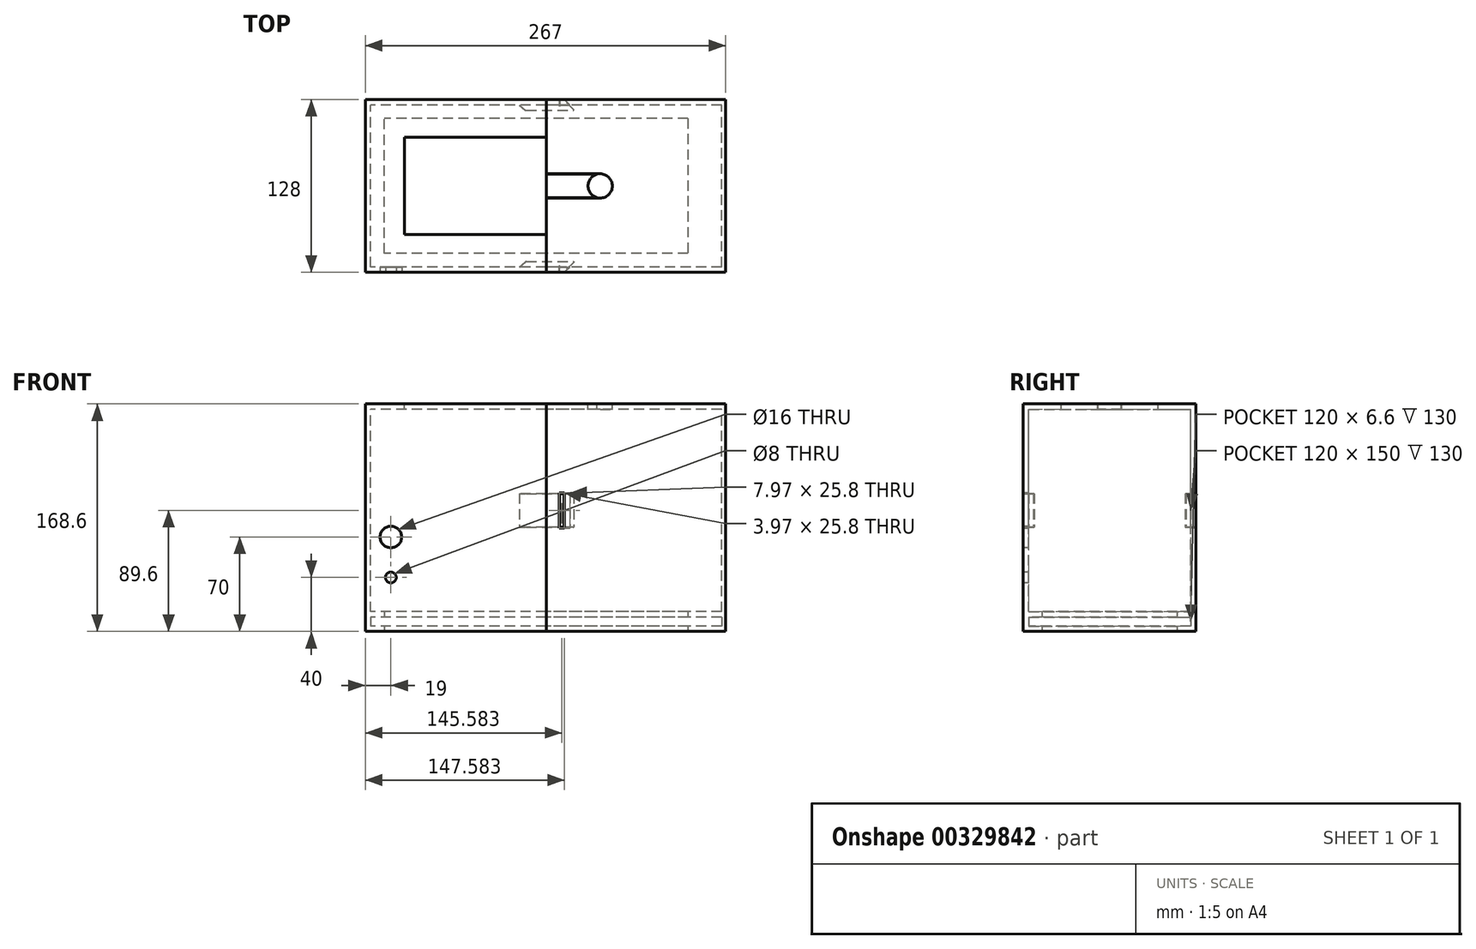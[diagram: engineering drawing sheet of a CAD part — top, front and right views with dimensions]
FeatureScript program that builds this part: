
annotation { "Feature Type Name" : "Feature", "Feature Type Description" : "" }
export const myFeature = defineFeature(function(context is Context, id is Id, definition is map)
    precondition{}
    {
        {
            assignVariable(context, id + "F0", {"name" : "InsideHeight", "anyValue" : 150});
        }
        {
            assignVariable(context, id + "F1", {"name" : "WallThickness", "anyValue" : 4});
        }
        {
            assignVariable(context, id + "F2", {"name" : "SlideGap", "anyValue" : 0.4});
        }
        {
            var Q0;
            Q0=qCreatedBy(makeId("Right.planeOp"),FACE);
            var sketch = newSketch(context, id + "F3", { "sketchPlane" : qUnion([Q0])});
            skLineSegment(sketch, "E0.top", {"start": v(0, 154) * mm, "end": v(64, 154) * mm});
            skLineSegment(sketch, "E0.left", {"start": v(0, 0) * mm, "end": v(0, 154) * mm});
            skLineSegment(sketch, "E1", {"start": v(4, 0) * mm, "end": v(4, 150) * mm});
            skLineSegment(sketch, "E2", {"start": v(4, 150) * mm, "end": v(64, 150) * mm});
            skLineSegment(sketch, "E3", {"start": v(4, 0) * mm, "end": v(14, 0) * mm});
            skLineSegment(sketch, "E4", {"start": v(14, 0) * mm, "end": v(14, -4) * mm});
            skLineSegment(sketch, "E5", {"start": v(14, -4) * mm, "end": v(4, -4) * mm});
            skLineSegment(sketch, "E6", {"start": v(4, -4) * mm, "end": v(4, -10.6) * mm});
            skLineSegment(sketch, "E7", {"start": v(4, -10.6) * mm, "end": v(14, -10.6) * mm});
            skLineSegment(sketch, "E8", {"start": v(14, -10.6) * mm, "end": v(14, -14.6) * mm});
            skLineSegment(sketch, "E9", {"start": v(14, -14.6) * mm, "end": v(0, -14.6) * mm});
            skLineSegment(sketch, "E10", {"start": v(0, -14.6) * mm, "end": v(0, 0) * mm});
            skLineSegment(sketch, "E11", {"start": v(64, 154) * mm, "end": v(64, 150) * mm, "construction": true});
            skLineSegment(sketch, "E12.MirrorCS", {"start": v(128, 154) * mm, "end": v(64, 154) * mm});
            skLineSegment(sketch, "E13.MirrorCS", {"start": v(124, 150) * mm, "end": v(64, 150) * mm});
            skLineSegment(sketch, "E14.MirrorCS", {"start": v(124, 0) * mm, "end": v(124, 150) * mm});
            skLineSegment(sketch, "E15.MirrorCS", {"start": v(128, 0) * mm, "end": v(128, 154) * mm});
            skLineSegment(sketch, "E16.MirrorCS", {"start": v(128, -14.6) * mm, "end": v(128, 0) * mm});
            skLineSegment(sketch, "E17.MirrorCS", {"start": v(114, -14.6) * mm, "end": v(128, -14.6) * mm});
            skLineSegment(sketch, "E18.MirrorCS", {"start": v(114, -10.6) * mm, "end": v(114, -14.6) * mm});
            skLineSegment(sketch, "E19.MirrorCS", {"start": v(124, -10.6) * mm, "end": v(114, -10.6) * mm});
            skLineSegment(sketch, "E20.MirrorCS", {"start": v(124, -4) * mm, "end": v(124, -10.6) * mm});
            skLineSegment(sketch, "E21.MirrorCS", {"start": v(114, -4) * mm, "end": v(124, -4) * mm});
            skLineSegment(sketch, "E22.MirrorCS", {"start": v(114, 0) * mm, "end": v(114, -4) * mm});
            skLineSegment(sketch, "E23.MirrorCS", {"start": v(124, 0) * mm, "end": v(114, 0) * mm});
            skLineSegment(sketch, "E24", {"start": v(4, -7.3) * mm, "end": v(0, -7.3) * mm, "construction": true});
            skSolve(sketch);
        }
        {
            var Q0;
            Q0 = qSketchRegion(id + "F3", true);
            extrude(context, id + "F4", {"entities" : qUnion([Q0]), "depth" : 130 * mm, "offsetDistance" : 25 * mm});
        }
        {
            var Q0;
            Q0=makeQuery(id+"F4.opExtrude","CAP_FACE",FACE,{"disambiguationData":[OSD([sQuery(id+"F3.wireOp",EDGE,"E0.top"),sQuery(id+"F3.wireOp",EDGE,"E0.left"),sQuery(id+"F3.wireOp",EDGE,"E0.right"),sQuery(id+"F3.wireOp",EDGE,"8XVz9hmB-15gg-s7JK-XLWV-TxlLlYY56E4R"),sQuery(id+"F3.wireOp",EDGE,"E1"),sQuery(id+"F3.wireOp",EDGE,"E2"),sQuery(id+"F3.wireOp",EDGE,"x6d7EpG5-ogLQ-dseG-wOhr-lL4PzdnoVMk9"),sQuery(id+"F3.wireOp",EDGE,"GP6dVw60-cyKg-IaOy-Ul32-FflkX6cR7JPA")])],"isStart":true});
            var sketch = newSketch(context, id + "F5", { "sketchPlane" : qUnion([Q0])});
            skLineSegment(sketch, "E25.bottom", {"start": v(0, 154) * mm, "end": v(-128, 154) * mm});
            skLineSegment(sketch, "E25.top", {"start": v(0, -14.6) * mm, "end": v(-128, -14.6) * mm});
            skLineSegment(sketch, "E25.left", {"start": v(0, 154) * mm, "end": v(0, -14.6) * mm});
            skLineSegment(sketch, "E25.right", {"start": v(-128, 154) * mm, "end": v(-128, -14.6) * mm});
            skSolve(sketch);
        }
        {
            var Q0;
            Q0 = qSketchRegion(id + "F5", true);
            extrude(context, id + "F6", {"entities" : qUnion([Q0]), "operationType" : NewBodyOperationType.ADD, "depth" : (getVariable(context, 'WallThickness')) * mm, "offsetDistance" : 25 * mm});
        }
        {
            var Q0;
            Q0=makeQuery(id+"F4.opExtrude","SWEPT_FACE",FACE,{"disambiguationData":[OSD([sQuery(id+"F3.wireOp",EDGE,"E2"),sQuery(id+"F3.wireOp",EDGE,"E13.MirrorCS")])]});
            cPlane(context, id + "F7", {"entities" : qUnion([Q0]), "cplaneType" : CPlaneType.OFFSET, "offset" : (getVariable(context, 'InsideHeight') / 2) * mm, "width" : 150 * mm, "height" : 150 * mm});
        }
        {
            var Q0;
            Q0=qCreatedBy(id+"F7.planeOp",FACE);
            var sketch = newSketch(context, id + "F8", { "sketchPlane" : qUnion([Q0])});
            skLineSegment(sketch, "E26", {"start": v(130, -120) * mm, "end": v(150.5, -120) * mm});
            skLineSegment(sketch, "E27", {"start": v(150.5, -120) * mm, "end": v(150.5, -120.5) * mm});
            skLineSegment(sketch, "E28", {"start": v(150.5, -120.5) * mm, "end": v(143, -128) * mm});
            skLineSegment(sketch, "E29", {"start": v(140, -128) * mm, "end": v(140, -124) * mm});
            skLineSegment(sketch, "E30", {"start": v(140, -124) * mm, "end": v(130, -124) * mm});
            skLineSegment(sketch, "E31", {"start": v(-4, -64) * mm, "end": v(0, -64) * mm, "construction": true});
            skLineSegment(sketch, "E32", {"start": v(140, -128) * mm, "end": v(143, -128) * mm});
            skPoint(sketch, "E33.orphan", {"position": v(140, -131) * mm});
            skLineSegment(sketch, "E34", {"start": v(130, -124) * mm, "end": v(110, -124) * mm});
            skLineSegment(sketch, "E35", {"start": v(110, -124) * mm, "end": v(115, -120) * mm});
            skLineSegment(sketch, "E36", {"start": v(115, -120) * mm, "end": v(130, -120) * mm});
            skLineSegment(sketch, "E37.MirrorCS", {"start": v(150.5, -7.5) * mm, "end": v(143, 0) * mm});
            skLineSegment(sketch, "E38.MirrorCS", {"start": v(140, 0) * mm, "end": v(143, 0) * mm});
            skLineSegment(sketch, "E39.MirrorCS", {"start": v(140, 0) * mm, "end": v(140, -4) * mm});
            skLineSegment(sketch, "E40.MirrorCS", {"start": v(140, -4) * mm, "end": v(130, -4) * mm});
            skLineSegment(sketch, "E41.MirrorCS", {"start": v(130, -4) * mm, "end": v(110, -4) * mm});
            skLineSegment(sketch, "E42.MirrorCS", {"start": v(110, -4) * mm, "end": v(115, -8) * mm});
            skLineSegment(sketch, "E43.MirrorCS", {"start": v(115, -8) * mm, "end": v(130, -8) * mm});
            skLineSegment(sketch, "E44.MirrorCS", {"start": v(130, -8) * mm, "end": v(150.5, -8) * mm});
            skLineSegment(sketch, "E45.MirrorCS", {"start": v(150.5, -8) * mm, "end": v(150.5, -7.5) * mm});
            skSolve(sketch);
        }
        {
            var Q0;
            Q0 = qSketchRegion(id + "F8", true);
            var Q1;
            Q1=makeQuery(id+"F6.boolean.opBoolean","MERGE",FACE,{"derivedFrom":[makeQuery(id+"F4.opExtrude","SWEPT_FACE",FACE,{"disambiguationData":[OSD([sQuery(id+"F3.wireOp",EDGE,"E0.top")])]}),makeQuery(id+"F6.opExtrude","SWEPT_FACE",FACE,{"disambiguationData":[OSD([sQuery(id+"F5.wireOp",EDGE,"WYE85QNL-GnE7-bL8G-Y7DR-a2gwiA7N3Xrg.bottom")])]})]});
            extrude(context, id + "F9", {"entities" : qUnion([Q0]), "operationType" : NewBodyOperationType.ADD, "oppositeDirection" : true, "depth" : 25 * mm, "endBoundEntityFace" : qUnion([Q1]), "offsetDistance" : 25 * mm, "symmetric" : true});
        }
        {
            var Q0;
            Q0=makeQuery(id+"F6.boolean.opBoolean","MERGE",FACE,{"derivedFrom":[makeQuery(id+"F4.opExtrude","SWEPT_FACE",FACE,{"disambiguationData":[OSD([sQuery(id+"F3.wireOp",EDGE,"E0.left"),sQuery(id+"F3.wireOp",EDGE,"E10")])]}),makeQuery(id+"F6.opExtrude","SWEPT_FACE",FACE,{"disambiguationData":[OSD([sQuery(id+"F5.wireOp",EDGE,"E25.left")])]})]});
            var sketch = newSketch(context, id + "F10", { "sketchPlane" : qUnion([Q0])});
            skCircle(sketch, "E46", {"center": v(15, 25.4) * mm, "radius": 4 * mm});
            skLineSegment(sketch, "E47", {"start": v(15, 25.4) * mm, "end": v(15, 55.4) * mm, "construction": true});
            skCircle(sketch, "E48", {"center": v(15, 55.4) * mm, "radius": 8 * mm});
            skSolve(sketch);
        }
        {
            var Q0;
            Q0 = qSketchRegion(id + "F10", true);
            extrude(context, id + "F11", {"entities" : qUnion([Q0]), "operationType" : NewBodyOperationType.REMOVE, "endBound" : BoundingType.UP_TO_NEXT, "oppositeDirection" : true, "depth" : 25 * mm, "offsetDistance" : 25 * mm});
        }
        {
            var Q0;
            Q0=makeQuery(id+"F6.opExtrude","CAP_FACE",FACE,{"disambiguationData":[OSD([sQuery(id+"F5.wireOp",EDGE,"E25.bottom"),sQuery(id+"F5.wireOp",EDGE,"E25.top"),sQuery(id+"F5.wireOp",EDGE,"E25.left"),sQuery(id+"F5.wireOp",EDGE,"E25.right")])],"isStart":true});
            var sketch = newSketch(context, id + "F12", { "sketchPlane" : qUnion([Q0])});
            skLineSegment(sketch, "E49.bottom", {"start": v(14, 0) * mm, "end": v(114, 0) * mm});
            skLineSegment(sketch, "E49.top", {"start": v(14, -4) * mm, "end": v(114, -4) * mm});
            skLineSegment(sketch, "E49.left", {"start": v(14, 0) * mm, "end": v(14, -4) * mm});
            skLineSegment(sketch, "E49.right", {"start": v(114, 0) * mm, "end": v(114, -4) * mm});
            skLineSegment(sketch, "E50.bottom", {"start": v(114, -10.6) * mm, "end": v(14, -10.6) * mm});
            skLineSegment(sketch, "E50.top", {"start": v(114, -14.6) * mm, "end": v(14, -14.6) * mm});
            skLineSegment(sketch, "E50.left", {"start": v(114, -10.6) * mm, "end": v(114, -14.6) * mm});
            skLineSegment(sketch, "E50.right", {"start": v(14, -10.6) * mm, "end": v(14, -14.6) * mm});
            skSolve(sketch);
        }
        {
            var Q0;
            Q0 = qSketchRegion(id + "F12", true);
            extrude(context, id + "F13", {"entities" : qUnion([Q0]), "operationType" : NewBodyOperationType.ADD, "depth" : 10 * mm, "offsetDistance" : 25 * mm});
        }
        {
            var Q0;
            Q0=makeQuery(id+"F4.opExtrude","CAP_FACE",FACE,{"disambiguationData":[OSD([sQuery(id+"F3.wireOp",EDGE,"E0.top"),sQuery(id+"F3.wireOp",EDGE,"E0.left"),sQuery(id+"F3.wireOp",EDGE,"E1"),sQuery(id+"F3.wireOp",EDGE,"E2"),sQuery(id+"F3.wireOp",EDGE,"E3"),sQuery(id+"F3.wireOp",EDGE,"E4"),sQuery(id+"F3.wireOp",EDGE,"E5"),sQuery(id+"F3.wireOp",EDGE,"E6"),sQuery(id+"F3.wireOp",EDGE,"E7"),sQuery(id+"F3.wireOp",EDGE,"E8"),sQuery(id+"F3.wireOp",EDGE,"E9"),sQuery(id+"F3.wireOp",EDGE,"E10"),sQuery(id+"F3.wireOp",EDGE,"E12.MirrorCS"),sQuery(id+"F3.wireOp",EDGE,"E13.MirrorCS"),sQuery(id+"F3.wireOp",EDGE,"E14.MirrorCS"),sQuery(id+"F3.wireOp",EDGE,"E15.MirrorCS"),sQuery(id+"F3.wireOp",EDGE,"E16.MirrorCS"),sQuery(id+"F3.wireOp",EDGE,"E17.MirrorCS"),sQuery(id+"F3.wireOp",EDGE,"E18.MirrorCS"),sQuery(id+"F3.wireOp",EDGE,"E19.MirrorCS"),sQuery(id+"F3.wireOp",EDGE,"E20.MirrorCS"),sQuery(id+"F3.wireOp",EDGE,"E21.MirrorCS"),sQuery(id+"F3.wireOp",EDGE,"E22.MirrorCS"),sQuery(id+"F3.wireOp",EDGE,"E23.MirrorCS")])],"isStart":false});
            extrude(context, id + "F14", {"entities" : qUnion([Q0]), "depth" : 130 * mm, "offsetDistance" : 25 * mm});
        }
        {
            var Q0;
            Q0=makeQuery(id+"F14.opExtrude","CAP_FACE",FACE,{"disambiguationData":[OSD([sQuery(id+"F3.wireOp",EDGE,"E0.top"),sQuery(id+"F3.wireOp",EDGE,"E0.left"),sQuery(id+"F3.wireOp",EDGE,"E1"),sQuery(id+"F3.wireOp",EDGE,"E2"),sQuery(id+"F3.wireOp",EDGE,"E3"),sQuery(id+"F3.wireOp",EDGE,"E4"),sQuery(id+"F3.wireOp",EDGE,"E5"),sQuery(id+"F3.wireOp",EDGE,"E6"),sQuery(id+"F3.wireOp",EDGE,"E7"),sQuery(id+"F3.wireOp",EDGE,"E8"),sQuery(id+"F3.wireOp",EDGE,"E9"),sQuery(id+"F3.wireOp",EDGE,"E10"),sQuery(id+"F3.wireOp",EDGE,"E12.MirrorCS"),sQuery(id+"F3.wireOp",EDGE,"E13.MirrorCS"),sQuery(id+"F3.wireOp",EDGE,"E14.MirrorCS"),sQuery(id+"F3.wireOp",EDGE,"E15.MirrorCS"),sQuery(id+"F3.wireOp",EDGE,"E16.MirrorCS"),sQuery(id+"F3.wireOp",EDGE,"E17.MirrorCS"),sQuery(id+"F3.wireOp",EDGE,"E18.MirrorCS"),sQuery(id+"F3.wireOp",EDGE,"E19.MirrorCS"),sQuery(id+"F3.wireOp",EDGE,"E20.MirrorCS"),sQuery(id+"F3.wireOp",EDGE,"E21.MirrorCS"),sQuery(id+"F3.wireOp",EDGE,"E22.MirrorCS"),sQuery(id+"F3.wireOp",EDGE,"E23.MirrorCS")])],"isStart":false});
            var sketch = newSketch(context, id + "F15", { "sketchPlane" : qUnion([Q0])});
            skLineSegment(sketch, "E51.bottom", {"start": v(0, 154) * mm, "end": v(128, 154) * mm});
            skLineSegment(sketch, "E51.top", {"start": v(0, -14.6) * mm, "end": v(128, -14.6) * mm});
            skLineSegment(sketch, "E51.left", {"start": v(0, 154) * mm, "end": v(0, -14.6) * mm});
            skLineSegment(sketch, "E51.right", {"start": v(128, 154) * mm, "end": v(128, -14.6) * mm});
            skSolve(sketch);
        }
        {
            var Q0;
            Q0 = qSketchRegion(id + "F15", true);
            extrude(context, id + "F16", {"entities" : qUnion([Q0]), "operationType" : NewBodyOperationType.ADD, "depth" : 3 * mm, "offsetDistance" : 25 * mm});
        }
        {
            var Q0;
            Q0=makeQuery(id+"F4.opExtrude","SWEPT_BODY",BODY,{"disambiguationData":[OSD([sQuery(id+"F3.wireOp",EDGE,"E0.top"),sQuery(id+"F3.wireOp",EDGE,"E0.left"),sQuery(id+"F3.wireOp",EDGE,"E1"),sQuery(id+"F3.wireOp",EDGE,"E2"),sQuery(id+"F3.wireOp",EDGE,"E3"),sQuery(id+"F3.wireOp",EDGE,"E4"),sQuery(id+"F3.wireOp",EDGE,"E5"),sQuery(id+"F3.wireOp",EDGE,"E6"),sQuery(id+"F3.wireOp",EDGE,"E7"),sQuery(id+"F3.wireOp",EDGE,"E8"),sQuery(id+"F3.wireOp",EDGE,"E9"),sQuery(id+"F3.wireOp",EDGE,"E10"),sQuery(id+"F3.wireOp",EDGE,"E12.MirrorCS"),sQuery(id+"F3.wireOp",EDGE,"E13.MirrorCS"),sQuery(id+"F3.wireOp",EDGE,"E14.MirrorCS"),sQuery(id+"F3.wireOp",EDGE,"E15.MirrorCS"),sQuery(id+"F3.wireOp",EDGE,"E16.MirrorCS"),sQuery(id+"F3.wireOp",EDGE,"E17.MirrorCS"),sQuery(id+"F3.wireOp",EDGE,"E18.MirrorCS"),sQuery(id+"F3.wireOp",EDGE,"E19.MirrorCS"),sQuery(id+"F3.wireOp",EDGE,"E20.MirrorCS"),sQuery(id+"F3.wireOp",EDGE,"E21.MirrorCS"),sQuery(id+"F3.wireOp",EDGE,"E22.MirrorCS"),sQuery(id+"F3.wireOp",EDGE,"E23.MirrorCS")])]});
            var Q1;
            Q1=makeQuery(id+"F14.opExtrude","SWEPT_BODY",BODY,{"disambiguationData":[OSD([sQuery(id+"F3.wireOp",EDGE,"E0.top"),sQuery(id+"F3.wireOp",EDGE,"E0.left"),sQuery(id+"F3.wireOp",EDGE,"E1"),sQuery(id+"F3.wireOp",EDGE,"E2"),sQuery(id+"F3.wireOp",EDGE,"E3"),sQuery(id+"F3.wireOp",EDGE,"E4"),sQuery(id+"F3.wireOp",EDGE,"E5"),sQuery(id+"F3.wireOp",EDGE,"E6"),sQuery(id+"F3.wireOp",EDGE,"E7"),sQuery(id+"F3.wireOp",EDGE,"E8"),sQuery(id+"F3.wireOp",EDGE,"E9"),sQuery(id+"F3.wireOp",EDGE,"E10"),sQuery(id+"F3.wireOp",EDGE,"E12.MirrorCS"),sQuery(id+"F3.wireOp",EDGE,"E13.MirrorCS"),sQuery(id+"F3.wireOp",EDGE,"E14.MirrorCS"),sQuery(id+"F3.wireOp",EDGE,"E15.MirrorCS"),sQuery(id+"F3.wireOp",EDGE,"E16.MirrorCS"),sQuery(id+"F3.wireOp",EDGE,"E17.MirrorCS"),sQuery(id+"F3.wireOp",EDGE,"E18.MirrorCS"),sQuery(id+"F3.wireOp",EDGE,"E19.MirrorCS"),sQuery(id+"F3.wireOp",EDGE,"E20.MirrorCS"),sQuery(id+"F3.wireOp",EDGE,"E21.MirrorCS"),sQuery(id+"F3.wireOp",EDGE,"E22.MirrorCS"),sQuery(id+"F3.wireOp",EDGE,"E23.MirrorCS")])]});
            var Q2;
            Q2=makeQuery(id+"F9.opExtrude","SWEPT_FACE",FACE,{"disambiguationData":[OSD([sQuery(id+"F8.wireOp",EDGE,"E39.MirrorCS")])]});
            var Q3;
            Q3=makeQuery(id+"F9.opExtrude","SWEPT_FACE",FACE,{"disambiguationData":[OSD([sQuery(id+"F8.wireOp",EDGE,"E38.MirrorCS")])]});
            var Q4;
            Q4=makeQuery(id+"F9.opExtrude","SWEPT_FACE",FACE,{"disambiguationData":[OSD([sQuery(id+"F8.wireOp",EDGE,"E37.MirrorCS")])]});
            var Q5;
            Q5=makeQuery(id+"F9.opExtrude","SWEPT_FACE",FACE,{"disambiguationData":[OSD([sQuery(id+"F8.wireOp",EDGE,"E43.MirrorCS"),sQuery(id+"F8.wireOp",EDGE,"E44.MirrorCS")])]});
            var Q6;
            Q6=makeQuery(id+"F9.opExtrude","CAP_FACE",FACE,{"disambiguationData":[OSD([sQuery(id+"F8.wireOp",EDGE,"E37.MirrorCS"),sQuery(id+"F8.wireOp",EDGE,"E38.MirrorCS"),sQuery(id+"F8.wireOp",EDGE,"E39.MirrorCS"),sQuery(id+"F8.wireOp",EDGE,"E40.MirrorCS"),sQuery(id+"F8.wireOp",EDGE,"E41.MirrorCS"),sQuery(id+"F8.wireOp",EDGE,"E42.MirrorCS"),sQuery(id+"F8.wireOp",EDGE,"E43.MirrorCS"),sQuery(id+"F8.wireOp",EDGE,"E44.MirrorCS"),sQuery(id+"F8.wireOp",EDGE,"E45.MirrorCS")])],"isStart":false});
            var Q7;
            Q7=makeQuery(id+"F9.opExtrude","CAP_FACE",FACE,{"disambiguationData":[OSD([sQuery(id+"F8.wireOp",EDGE,"E37.MirrorCS"),sQuery(id+"F8.wireOp",EDGE,"E38.MirrorCS"),sQuery(id+"F8.wireOp",EDGE,"E39.MirrorCS"),sQuery(id+"F8.wireOp",EDGE,"E40.MirrorCS"),sQuery(id+"F8.wireOp",EDGE,"E41.MirrorCS"),sQuery(id+"F8.wireOp",EDGE,"E42.MirrorCS"),sQuery(id+"F8.wireOp",EDGE,"E43.MirrorCS"),sQuery(id+"F8.wireOp",EDGE,"E44.MirrorCS"),sQuery(id+"F8.wireOp",EDGE,"E45.MirrorCS")])],"isStart":true});
            var Q8;
            Q8=makeQuery(id+"F9.opExtrude","CAP_FACE",FACE,{"disambiguationData":[OSD([sQuery(id+"F8.wireOp",EDGE,"E26"),sQuery(id+"F8.wireOp",EDGE,"E27"),sQuery(id+"F8.wireOp",EDGE,"E28"),sQuery(id+"F8.wireOp",EDGE,"E29"),sQuery(id+"F8.wireOp",EDGE,"E30"),sQuery(id+"F8.wireOp",EDGE,"E32"),sQuery(id+"F8.wireOp",EDGE,"E34"),sQuery(id+"F8.wireOp",EDGE,"E35"),sQuery(id+"F8.wireOp",EDGE,"E36")])],"isStart":false});
            var Q9;
            Q9=makeQuery(id+"F9.opExtrude","SWEPT_FACE",FACE,{"disambiguationData":[OSD([sQuery(id+"F8.wireOp",EDGE,"E28")])]});
            var Q10;
            Q10=makeQuery(id+"F9.opExtrude","SWEPT_FACE",FACE,{"disambiguationData":[OSD([sQuery(id+"F8.wireOp",EDGE,"E32")])]});
            var Q11;
            Q11=makeQuery(id+"F9.opExtrude","SWEPT_FACE",FACE,{"disambiguationData":[OSD([sQuery(id+"F8.wireOp",EDGE,"E29")])]});
            var Q12;
            Q12=makeQuery(id+"F9.opExtrude","CAP_FACE",FACE,{"disambiguationData":[OSD([sQuery(id+"F8.wireOp",EDGE,"E26"),sQuery(id+"F8.wireOp",EDGE,"E27"),sQuery(id+"F8.wireOp",EDGE,"E28"),sQuery(id+"F8.wireOp",EDGE,"E29"),sQuery(id+"F8.wireOp",EDGE,"E30"),sQuery(id+"F8.wireOp",EDGE,"E32"),sQuery(id+"F8.wireOp",EDGE,"E34"),sQuery(id+"F8.wireOp",EDGE,"E35"),sQuery(id+"F8.wireOp",EDGE,"E36")])],"isStart":true});
            var Q13;
            Q13=makeQuery(id+"F9.opExtrude","SWEPT_FACE",FACE,{"disambiguationData":[OSD([sQuery(id+"F8.wireOp",EDGE,"E27")])]});
            var Q14;
            Q14=makeQuery(id+"F9.opExtrude","SWEPT_FACE",FACE,{"disambiguationData":[OSD([sQuery(id+"F8.wireOp",EDGE,"E26"),sQuery(id+"F8.wireOp",EDGE,"E36")])]});
            booleanBodies(context, id + "F17", {"operationType" : BooleanOperationType.SUBTRACTION, "tools" : qUnion([Q0]), "targets" : qUnion([Q1]), "offset" : true, "entitiesToOffset" : qUnion([Q2, Q3, Q4, Q5, Q6, Q7, Q8, Q9, Q10, Q11, Q12, Q13, Q14]), "offsetDistance" : (getVariable(context, 'SlideGap')) * mm, "keepTools" : true});
        }
        {
            var Q0;
            {var subQ0=sQuery(id+"F8.wireOp",EDGE,"E34");var subQ1=sQuery(id+"F8.wireOp",EDGE,"E30");Q0=makeQuery(id+"F9.boolean.opBoolean","SPLIT",EDGE,{"disambiguationData":[topologyDisambiguationEdgeConnected([makeQuery(id+"F4.opExtrude","SWEPT_FACE",FACE,{"disambiguationData":[OSD([sQuery(id+"F3.wireOp",EDGE,"E14.MirrorCS")])]})])],"derivedFrom":makeQuery(id+"F9.opExtrude","CAP_EDGE",EDGE,{"disambiguationData":[OSD([subQ1,subQ0])],"isStart":false})});}
            var Q1;
            Q1=makeQuery(id+"F9.opExtrude","SWEPT_EDGE",EDGE,{"disambiguationData":[OSD([sQuery(id+"F8.wireOp",EDGE,"E34"),sQuery(id+"F8.wireOp",EDGE,"E35")])]});
            var Q2;
            {var subQ0=sQuery(id+"F8.wireOp",EDGE,"E34");var subQ1=sQuery(id+"F8.wireOp",EDGE,"E30");Q2=makeQuery(id+"F9.boolean.opBoolean","SPLIT",EDGE,{"disambiguationData":[topologyDisambiguationEdgeConnected([makeQuery(id+"F4.opExtrude","SWEPT_FACE",FACE,{"disambiguationData":[OSD([sQuery(id+"F3.wireOp",EDGE,"E14.MirrorCS")])]})])],"derivedFrom":makeQuery(id+"F9.opExtrude","CAP_EDGE",EDGE,{"disambiguationData":[OSD([subQ1,subQ0])],"isStart":true})});}
            var Q3;
            Q3=makeQuery(id+"F9.opExtrude","SWEPT_EDGE",EDGE,{"disambiguationData":[OSD([sQuery(id+"F8.wireOp",EDGE,"E35"),sQuery(id+"F8.wireOp",EDGE,"E36")])]});
            var Q4;
            Q4=makeQuery(id+"F9.opExtrude","SWEPT_EDGE",EDGE,{"disambiguationData":[OSD([sQuery(id+"F8.wireOp",EDGE,"E42.MirrorCS"),sQuery(id+"F8.wireOp",EDGE,"E43.MirrorCS")])]});
            var Q5;
            Q5=makeQuery(id+"F9.opExtrude","SWEPT_EDGE",EDGE,{"disambiguationData":[OSD([sQuery(id+"F8.wireOp",EDGE,"E41.MirrorCS"),sQuery(id+"F8.wireOp",EDGE,"E42.MirrorCS")])]});
            var Q6;
            {var subQ0=sQuery(id+"F8.wireOp",EDGE,"E41.MirrorCS");var subQ1=sQuery(id+"F8.wireOp",EDGE,"E40.MirrorCS");Q6=makeQuery(id+"F9.boolean.opBoolean","SPLIT",EDGE,{"disambiguationData":[topologyDisambiguationEdgeConnected([makeQuery(id+"F4.opExtrude","SWEPT_FACE",FACE,{"disambiguationData":[OSD([sQuery(id+"F3.wireOp",EDGE,"E1")])]})])],"derivedFrom":makeQuery(id+"F9.opExtrude","CAP_EDGE",EDGE,{"disambiguationData":[OSD([subQ1,subQ0])],"isStart":false})});}
            var Q7;
            {var subQ0=sQuery(id+"F8.wireOp",EDGE,"E41.MirrorCS");var subQ1=sQuery(id+"F8.wireOp",EDGE,"E40.MirrorCS");Q7=makeQuery(id+"F9.boolean.opBoolean","SPLIT",EDGE,{"disambiguationData":[topologyDisambiguationEdgeConnected([makeQuery(id+"F4.opExtrude","SWEPT_FACE",FACE,{"disambiguationData":[OSD([sQuery(id+"F3.wireOp",EDGE,"E1")])]})])],"derivedFrom":makeQuery(id+"F9.opExtrude","CAP_EDGE",EDGE,{"disambiguationData":[OSD([subQ1,subQ0])],"isStart":true})});}
            fillet(context, id + "F18", {"entities" : qUnion([Q0, Q1, Q2, Q3, Q4, Q5, Q6, Q7]), "radius" : 1 * mm, "tangentPropagation" : true, "allowEdgeOverflow" : false});
        }
        {
            var Q0;
            Q0=makeQuery(id+"F16.opExtrude","CAP_FACE",FACE,{"disambiguationData":[OSD([sQuery(id+"F15.wireOp",EDGE,"E51.bottom"),sQuery(id+"F15.wireOp",EDGE,"E51.top"),sQuery(id+"F15.wireOp",EDGE,"E51.left"),sQuery(id+"F15.wireOp",EDGE,"E51.right")])],"isStart":true});
            var sketch = newSketch(context, id + "F19", { "sketchPlane" : qUnion([Q0])});
            skLineSegment(sketch, "E52.bottom", {"start": v(-114, 0) * mm, "end": v(-14, 0) * mm});
            skLineSegment(sketch, "E52.top", {"start": v(-114, -4) * mm, "end": v(-14, -4) * mm});
            skLineSegment(sketch, "E52.left", {"start": v(-114, 0) * mm, "end": v(-114, -4) * mm});
            skLineSegment(sketch, "E52.right", {"start": v(-14, 0) * mm, "end": v(-14, -4) * mm});
            skLineSegment(sketch, "E53.bottom", {"start": v(-14, -10.6) * mm, "end": v(-114, -10.6) * mm});
            skLineSegment(sketch, "E53.top", {"start": v(-14, -14.6) * mm, "end": v(-114, -14.6) * mm});
            skLineSegment(sketch, "E53.left", {"start": v(-14, -10.6) * mm, "end": v(-14, -14.6) * mm});
            skLineSegment(sketch, "E53.right", {"start": v(-114, -10.6) * mm, "end": v(-114, -14.6) * mm});
            skSolve(sketch);
        }
        {
            var Q0;
            Q0 = qSketchRegion(id + "F19", true);
            extrude(context, id + "F20", {"entities" : qUnion([Q0]), "operationType" : NewBodyOperationType.ADD, "depth" : 25 * mm, "offsetDistance" : 25 * mm});
        }
        {
            var Q0;
            {var subQ0=sQuery(id+"F5.wireOp",EDGE,"E25.bottom");var subQ1=sQuery(id+"F3.wireOp",EDGE,"E12.MirrorCS");var subQ2=sQuery(id+"F3.wireOp",EDGE,"E0.top");Q0=makeQuery(id+"F9.boolean.opBoolean","MERGE",FACE,{"derivedFrom":[makeQuery(id+"F6.boolean.opBoolean","MERGE",FACE,{"derivedFrom":[makeQuery(id+"F4.opExtrude","SWEPT_FACE",FACE,{"disambiguationData":[OSD([subQ2,subQ1])]}),makeQuery(id+"F6.opExtrude","SWEPT_FACE",FACE,{"disambiguationData":[OSD([subQ0])]})]}),makeQuery(id+"F9.opExtrude","CAP_FACE",FACE,{"disambiguationData":[OSD([subQ2,subQ1,subQ0]),OD(0.0)],"isStart":false}),makeQuery(id+"F9.opExtrude","CAP_FACE",FACE,{"disambiguationData":[OSD([subQ2,subQ1,subQ0]),OD(1.0)],"isStart":false})]});}
            var sketch = newSketch(context, id + "F21", { "sketchPlane" : qUnion([Q0])});
            skLineSegment(sketch, "E54.bottom", {"start": v(25, 100) * mm, "end": v(130, 100) * mm});
            skLineSegment(sketch, "E54.top", {"start": v(25, 28) * mm, "end": v(130, 28) * mm});
            skLineSegment(sketch, "E54.left", {"start": v(25, 100) * mm, "end": v(25, 28) * mm});
            skLineSegment(sketch, "E54.right", {"start": v(130, 100) * mm, "end": v(130, 28) * mm});
            skLineSegment(sketch, "E55", {"start": v(-4, 64) * mm, "end": v(25, 64) * mm, "construction": true});
            skSolve(sketch);
        }
        {
            var Q0;
            Q0 = qSketchRegion(id + "F21", true);
            extrude(context, id + "F22", {"entities" : qUnion([Q0]), "operationType" : NewBodyOperationType.REMOVE, "endBound" : BoundingType.UP_TO_NEXT, "oppositeDirection" : true, "depth" : 25 * mm, "offsetDistance" : 25 * mm});
        }
        {
            var Q0;
            Q0=makeQuery(id+"F16.boolean.opBoolean","MERGE",FACE,{"derivedFrom":[makeQuery(id+"FLr4bme93UtqGT1_1.opExtrude","SWEPT_FACE",FACE,{"disambiguationData":[OSD([sQuery(id+"FQV2HkQOvfL55he_1.wireOp",EDGE,"6ba534eb-66d4-458a-884e-e74db9a0ddee.11")])]}),makeQuery(id+"F16.opExtrude","SWEPT_FACE",FACE,{"disambiguationData":[OSD([sQuery(id+"F15.wireOp",EDGE,"E51.bottom")])]})]});
            var sketch = newSketch(context, id + "F23", { "sketchPlane" : qUnion([Q0])});
            skCircle(sketch, "E56", {"center": v(170, 64) * mm, "radius": 9 * mm});
            skLineSegment(sketch, "E57", {"start": v(170, 64) * mm, "end": v(130, 64) * mm, "construction": true});
            skSolve(sketch);
        }
        {
            var Q0;
            Q0 = qSketchRegion(id + "F23", true);
            extrude(context, id + "F24", {"entities" : qUnion([Q0]), "operationType" : NewBodyOperationType.REMOVE, "endBound" : BoundingType.UP_TO_NEXT, "oppositeDirection" : true, "depth" : 25 * mm, "offsetDistance" : 25 * mm});
        }
        {
            var Q0;
            Q0=makeQuery(id+"F16.boolean.opBoolean","MERGE",FACE,{"derivedFrom":[makeQuery(id+"FLr4bme93UtqGT1_1.opExtrude","SWEPT_FACE",FACE,{"disambiguationData":[OSD([sQuery(id+"FQV2HkQOvfL55he_1.wireOp",EDGE,"6ba534eb-66d4-458a-884e-e74db9a0ddee.11")])]}),makeQuery(id+"F16.opExtrude","SWEPT_FACE",FACE,{"disambiguationData":[OSD([sQuery(id+"F15.wireOp",EDGE,"E51.bottom")])]})]});
            var sketch = newSketch(context, id + "F25", { "sketchPlane" : qUnion([Q0])});
            skLineSegment(sketch, "E58.bottom", {"start": v(130, 73) * mm, "end": v(170, 73) * mm});
            skLineSegment(sketch, "E58.top", {"start": v(130, 72.7) * mm, "end": v(170, 72.7) * mm});
            skLineSegment(sketch, "E58.left", {"start": v(130, 73) * mm, "end": v(130, 72.7) * mm});
            skLineSegment(sketch, "E58.right", {"start": v(170, 73) * mm, "end": v(170, 72.7) * mm});
            skLineSegment(sketch, "E59.bottom", {"start": v(170, 55.3) * mm, "end": v(130, 55.3) * mm});
            skLineSegment(sketch, "E59.top", {"start": v(170, 55) * mm, "end": v(130, 55) * mm});
            skLineSegment(sketch, "E59.left", {"start": v(170, 55.3) * mm, "end": v(170, 55) * mm});
            skLineSegment(sketch, "E59.right", {"start": v(130, 55.3) * mm, "end": v(130, 55) * mm});
            skSolve(sketch);
        }
        {
            var Q0;
            Q0 = qSketchRegion(id + "F25", true);
            extrude(context, id + "F26", {"entities" : qUnion([Q0]), "operationType" : NewBodyOperationType.REMOVE, "endBound" : BoundingType.UP_TO_NEXT, "oppositeDirection" : true, "depth" : 25 * mm, "offsetDistance" : 25 * mm});
        }
    });
